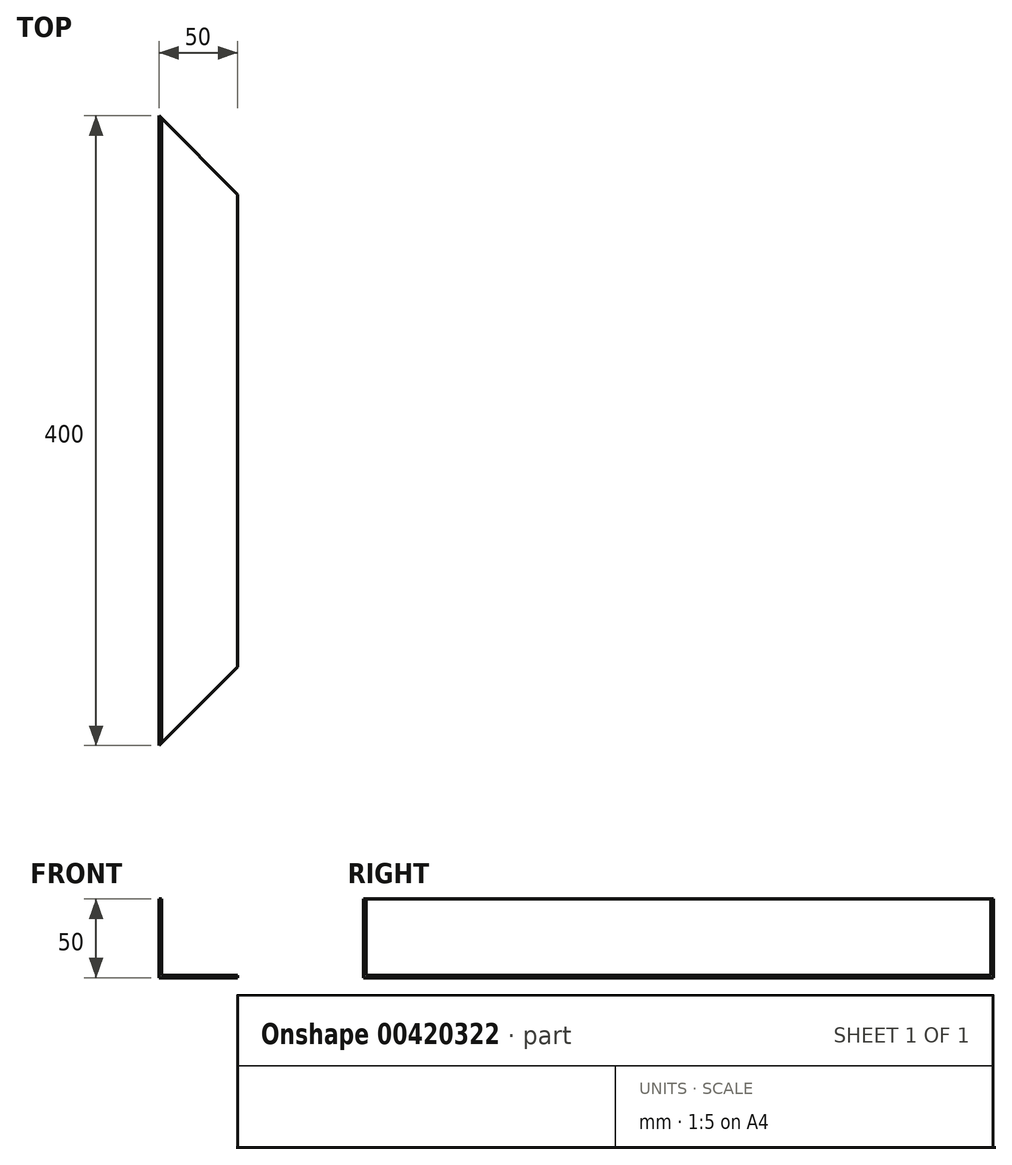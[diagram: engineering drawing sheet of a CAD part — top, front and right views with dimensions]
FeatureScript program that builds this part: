
annotation { "Feature Type Name" : "Feature", "Feature Type Description" : "" }
export const myFeature = defineFeature(function(context is Context, id is Id, definition is map)
    precondition{}
    {
        {
            var Q0;
            Q0=qCreatedBy(makeId("Front.planeOp"),FACE);
            var sketch = newSketch(context, id + "F0", { "sketchPlane" : qUnion([Q0])});
            skLineSegment(sketch, "E0.bottom", {"start": v(-33, 48.4) * mm, "end": v(-31.4, 48.4) * mm});
            skLineSegment(sketch, "E0.top", {"start": v(-33, -1.6) * mm, "end": v(-31.4, -1.6) * mm});
            skLineSegment(sketch, "E0.left", {"start": v(-33, 48.4) * mm, "end": v(-33, -1.6) * mm});
            skLineSegment(sketch, "E0.right", {"start": v(-31.4, 48.4) * mm, "end": v(-31.4, -1.6) * mm});
            skLineSegment(sketch, "E1.bottom", {"start": v(-33, -1.6) * mm, "end": v(17, -1.6) * mm});
            skLineSegment(sketch, "E1.top", {"start": v(-33, 0) * mm, "end": v(17, 0) * mm});
            skLineSegment(sketch, "E1.left", {"start": v(-33, -1.6) * mm, "end": v(-33, 0) * mm});
            skLineSegment(sketch, "E1.right", {"start": v(17, -1.6) * mm, "end": v(17, 0) * mm});
            skSolve(sketch);
        }
        {
            var Q0;
            Q0=qSketchRegion(id+"F0",true);
            extrude(context, id + "F1", {"entities" : qUnion([Q0]), "depth" : 400 * mm});
        }
        {
            var Q0;
            Q0=makeQuery(id+"F1.opExtrude","SWEPT_FACE",FACE,{"disambiguationData":[OSD([sQuery(id+"F0.wireOp",EDGE,"E1.bottom")])]});
            var sketch = newSketch(context, id + "F2", { "sketchPlane" : qUnion([Q0])});
            skLineSegment(sketch, "E2", {"start": v(-33, 0) * mm, "end": v(17, 50) * mm});
            skLineSegment(sketch, "E3", {"start": v(17, 50) * mm, "end": v(17, 0) * mm});
            skLineSegment(sketch, "E4", {"start": v(17, 0) * mm, "end": v(-33, 0) * mm});
            skSolve(sketch);
        }
        {
            var Q0;
            Q0=qSketchRegion(id+"F2",true);
            extrude(context, id + "F3", {"entities" : qUnion([Q0]), "operationType" : NewBodyOperationType.REMOVE, "endBound" : BoundingType.THROUGH_ALL, "oppositeDirection" : true, "depth" : 25 * mm});
        }
        {
            var Q0;
            Q0=makeQuery(id+"F1.opExtrude","SWEPT_FACE",FACE,{"disambiguationData":[OSD([sQuery(id+"F0.wireOp",EDGE,"E1.bottom")])]});
            var sketch = newSketch(context, id + "F4", { "sketchPlane" : qUnion([Q0])});
            skLineSegment(sketch, "E5", {"start": v(-33, 400) * mm, "end": v(17, 350) * mm});
            skLineSegment(sketch, "E6", {"start": v(17, 350) * mm, "end": v(17, 400) * mm});
            skLineSegment(sketch, "E7", {"start": v(17, 400) * mm, "end": v(-33, 400) * mm});
            skSolve(sketch);
        }
        {
            var Q0;
            Q0=qSketchRegion(id+"F4",true);
            extrude(context, id + "F5", {"entities" : qUnion([Q0]), "operationType" : NewBodyOperationType.REMOVE, "endBound" : BoundingType.THROUGH_ALL, "oppositeDirection" : true, "depth" : 25 * mm});
        }
    });
